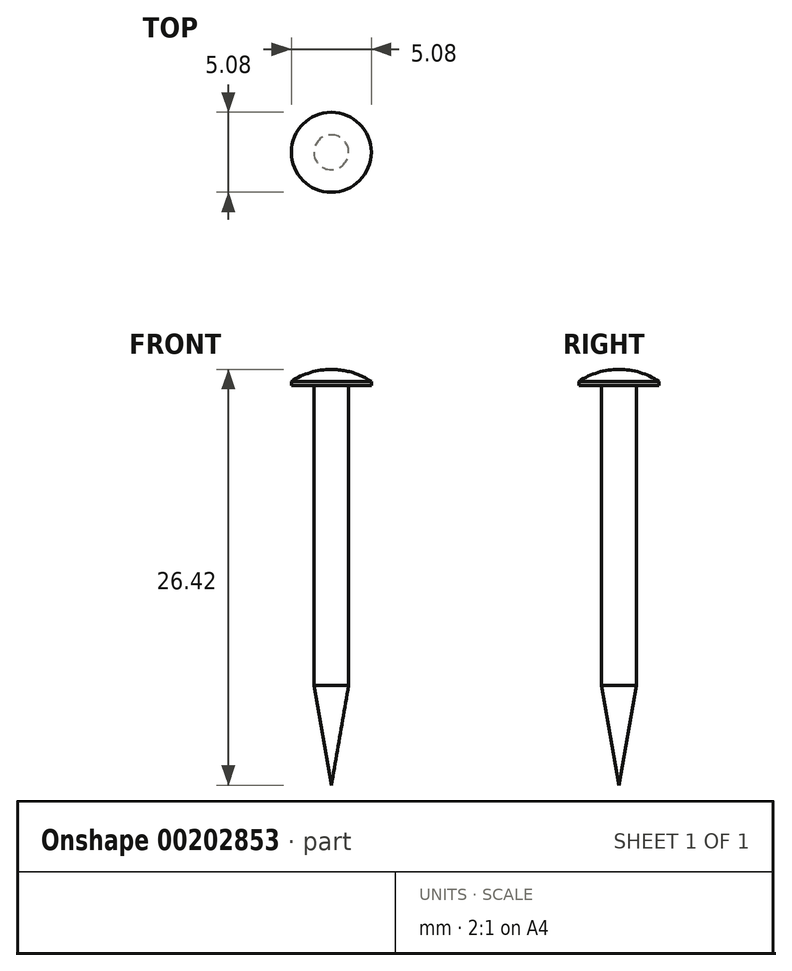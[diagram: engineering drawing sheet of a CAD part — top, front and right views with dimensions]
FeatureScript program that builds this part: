
annotation { "Feature Type Name" : "Feature", "Feature Type Description" : "" }
export const myFeature = defineFeature(function(context is Context, id is Id, definition is map)
    precondition{}
    {
        {
            var Q0;
            Q0=qCreatedBy(makeId("Front.planeOp"),FACE);
            var sketch = newSketch(context, id + "F0", { "sketchPlane" : qUnion([Q0])});
            skLineSegment(sketch, "E0", {"start": v(-1.1, 0) * mm, "end": v(-2.54, 0) * mm});
            skLineSegment(sketch, "E1", {"start": v(-1.1, 0) * mm, "end": v(-1.1, -19.05) * mm});
            skLineSegment(sketch, "E2", {"start": v(-1.1, -19.05) * mm, "end": v(0, -25.4) * mm});
            skLineSegment(sketch, "E3", {"start": v(0, 1.02) * mm, "end": v(0, -25.4) * mm});
            skLineSegment(sketch, "E4", {"start": v(-2.54, 0) * mm, "end": v(-2.54, 0.25) * mm});
            skArc(sketch, "E5", {"start": v(0, 1.02) * mm, "mid": v(-1.33, 0.82) * mm, "end": v(-2.54, 0.25) * mm});
            skSolve(sketch);
        }
        {
            var Q0;
            Q0=qSketchRegion(id+"F0",true);
            var Q1;
            Q1=sQuery(id+"F0.wireOp",EDGE,"E3");
            revolve(context, id + "F1", {"entities" : qUnion([Q0]), "axis" : qUnion([Q1]), "revolveType" : RevolveType.FULL});
        }
    });
